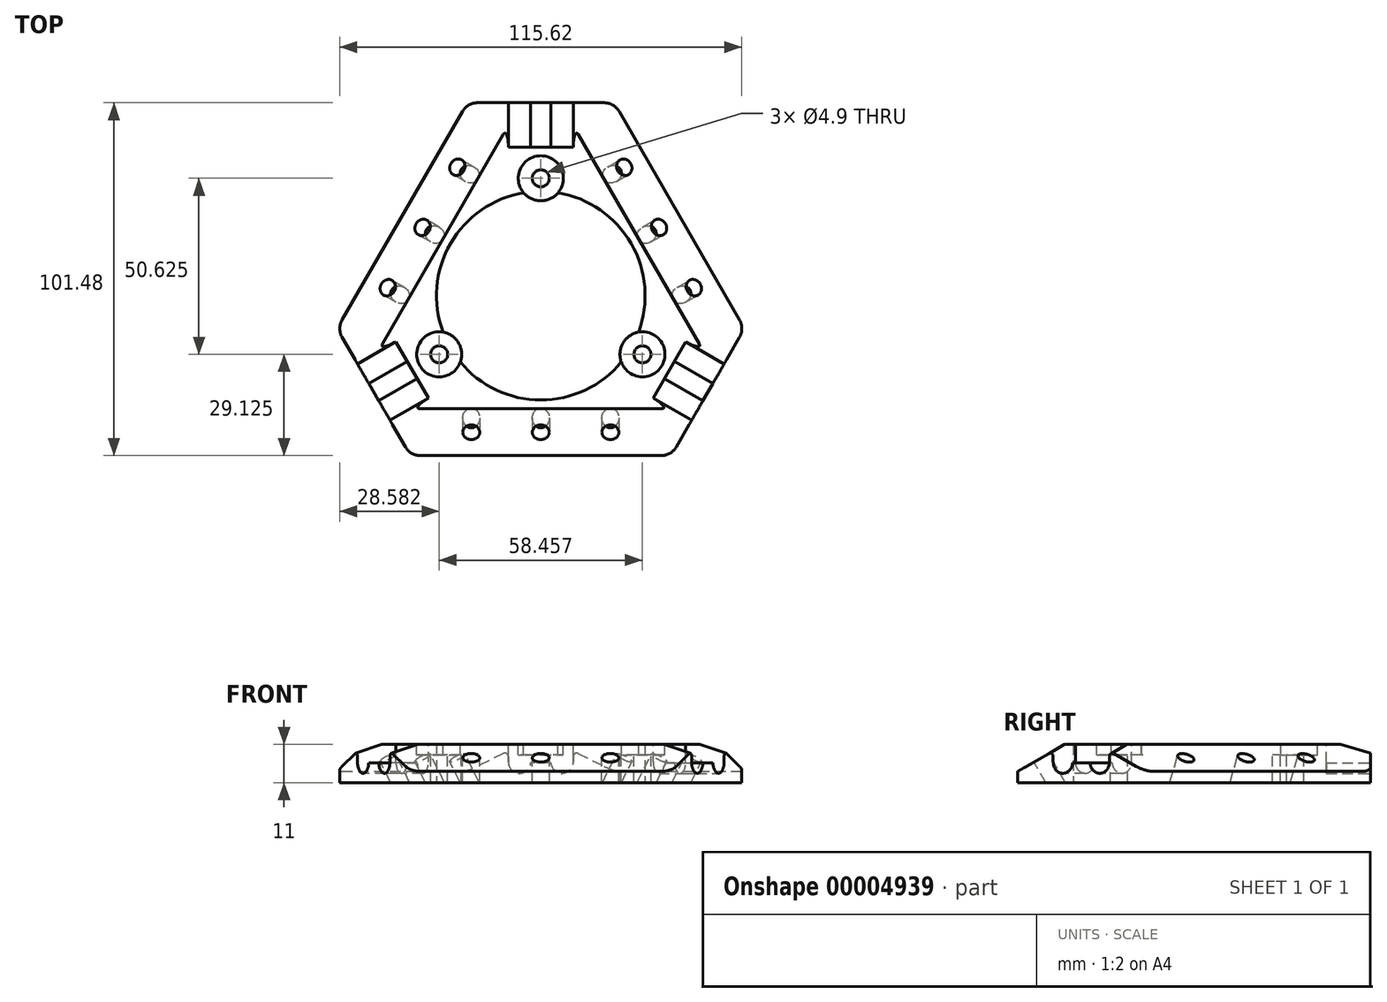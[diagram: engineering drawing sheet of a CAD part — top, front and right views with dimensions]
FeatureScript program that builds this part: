
annotation { "Feature Type Name" : "Feature", "Feature Type Description" : "" }
export const myFeature = defineFeature(function(context is Context, id is Id, definition is map)
    precondition{}
    {
        {
            var Q0;
            Q0=qCreatedBy(makeId("Top.planeOp"),FACE);
            var sketch = newSketch(context, id + "F0", { "sketchPlane" : qUnion([Q0])});
            skArc(sketch, "E0", {"start": v(-25.98, -15) * mm, "mid": v(0, -30) * mm, "end": v(25.98, -15) * mm});
            skLineSegment(sketch, "E1", {"start": v(-37.5, -46) * mm, "end": v(37.5, -46) * mm});
            skLineSegment(sketch, "E2", {"start": v(37.5, -46) * mm, "end": v(48.04, -27.74) * mm});
            skLineSegment(sketch, "E3", {"start": v(48.04, -27.74) * mm, "end": v(25.98, -15) * mm});
            skLineSegment(sketch, "E4", {"start": v(25.98, -15) * mm, "end": v(0, 0) * mm, "construction": true});
            skLineSegment(sketch, "E5", {"start": v(0, 0) * mm, "end": v(0, -46) * mm, "construction": true});
            skLineSegment(sketch, "E6.0.MirrorCS", {"start": v(-37.5, -46) * mm, "end": v(-48.04, -27.74) * mm});
            skLineSegment(sketch, "E6.1.MirrorCS", {"start": v(-48.04, -27.74) * mm, "end": v(-25.98, -15) * mm});
            skPoint(sketch, "E7", {"position": v(0, -30) * mm});
            skSolve(sketch);
        }
        {
            var Q0;
            Q0 = qSketchRegion(id + "F0", true);
            extrude(context, id + "F1", {"entities" : qUnion([Q0]), "depth" : 8 * mm, "symmetric" : true});
        }
        {
            var Q0;
            Q0=qCreatedBy(makeId("Right.planeOp"),FACE);
            var sketch = newSketch(context, id + "F2", { "sketchPlane" : qUnion([Q0])});
            skLineSegment(sketch, "E8", {"start": v(0, 0) * mm, "end": v(-39.45, 0) * mm, "construction": true});
            skLineSegment(sketch, "E9", {"start": v(-46.38, -4) * mm, "end": v(-32.52, 4) * mm});
            skLineSegment(sketch, "E10.0", {"start": v(-46, 4) * mm, "end": v(-32.52, 4) * mm});
            skLineSegment(sketch, "E11", {"start": v(-46, 4) * mm, "end": v(-46.38, 4) * mm});
            skLineSegment(sketch, "E12", {"start": v(-46.38, 4) * mm, "end": v(-46.38, -4) * mm});
            skPoint(sketch, "E13.orphan", {"position": v(-27.74, 4) * mm});
            skSolve(sketch);
        }
        {
            var Q0;
            Q0 = qSketchRegion(id + "F2", true);
            extrude(context, id + "F3", {"entities" : qUnion([Q0]), "operationType" : NewBodyOperationType.REMOVE, "oppositeDirection" : true, "depth" : 100 * mm, "symmetric" : true});
        }
        {
            var Q0;
            Q0=makeQuery(id+"F1.opExtrude","CAP_FACE",FACE,{"disambiguationData":[OSD([sQuery(id+"F0.wireOp",EDGE,"E0"),sQuery(id+"F0.wireOp",EDGE,"E1"),sQuery(id+"F0.wireOp",EDGE,"E2"),sQuery(id+"F0.wireOp",EDGE,"E3"),sQuery(id+"F0.wireOp",EDGE,"E6.0.MirrorCS"),sQuery(id+"F0.wireOp",EDGE,"E6.1.MirrorCS")])],"isStart":true});
            var sketch = newSketch(context, id + "F4", { "sketchPlane" : qUnion([Q0])});
            skLineSegment(sketch, "E14.0", {"start": v(-37.5, 46) * mm, "end": v(-48.04, 27.74) * mm});
            skLineSegment(sketch, "E14.1", {"start": v(-37.5, 46) * mm, "end": v(37.5, 46) * mm});
            skLineSegment(sketch, "E14.2", {"start": v(37.5, 46) * mm, "end": v(48.04, 27.74) * mm});
            skLineSegment(sketch, "E14.3", {"start": v(48.04, 27.74) * mm, "end": v(25.98, 15) * mm});
            skArc(sketch, "E14.4", {"start": v(-25.98, 15) * mm, "mid": v(0, 30) * mm, "end": v(25.98, 15) * mm});
            skLineSegment(sketch, "E14.5", {"start": v(-48.04, 27.74) * mm, "end": v(-25.98, 15) * mm});
            skSolve(sketch);
        }
        {
            var Q0;
            Q0 = qSketchRegion(id + "F4", true);
            extrude(context, id + "F5", {"entities" : qUnion([Q0]), "operationType" : NewBodyOperationType.ADD, "depth" : 3 * mm});
        }
        {
            var Q0;
            Q0=makeQuery(id+"F3.boolean.opBoolean","COPY",FACE,{"derivedFrom":makeQuery(id+"F3.opExtrude","SWEPT_FACE",FACE,{"disambiguationData":[OSD([sQuery(id+"F2.wireOp",EDGE,"E9")])]})});
            var sketch = newSketch(context, id + "F6", { "sketchPlane" : qUnion([Q0])});
            skLineSegment(sketch, "E15", {"start": v(0, -26.16) * mm, "end": v(0, -41.73) * mm, "construction": true});
            skLineSegment(sketch, "E16", {"start": v(0, -33.95) * mm, "end": v(20, -33.95) * mm, "construction": true});
            skCircle(sketch, "E17", {"center": v(20, -33.95) * mm, "radius": 2.45 * mm});
            skCircle(sketch, "E18.0.MirrorC", {"center": v(-20, -33.95) * mm, "radius": 2.45 * mm});
            skCircle(sketch, "E19", {"center": v(0, -33.95) * mm, "radius": 2.45 * mm});
            skSolve(sketch);
        }
        {
            var Q0;
            Q0 = qSketchRegion(id + "F6", true);
            extrude(context, id + "F7", {"entities" : qUnion([Q0]), "operationType" : NewBodyOperationType.REMOVE, "endBound" : BoundingType.THROUGH_ALL, "oppositeDirection" : true, "depth" : 25 * mm});
        }
        {
            var Q0;
            Q0=makeQuery(id+"F5.boolean.opBoolean","MERGE",FACE,{"derivedFrom":[makeQuery(id+"F1.opExtrude","SWEPT_FACE",FACE,{"disambiguationData":[OSD([sQuery(id+"F0.wireOp",EDGE,"E2")])]}),makeQuery(id+"F5.opExtrude","SWEPT_FACE",FACE,{"disambiguationData":[OSD([sQuery(id+"F4.wireOp",EDGE,"E14.2")])]})]});
            var sketch = newSketch(context, id + "F8", { "sketchPlane" : qUnion([Q0])});
            skCircle(sketch, "E20", {"center": v(-6.1, -1.13) * mm, "radius": 3.23 * mm});
            skPoint(sketch, "E21", {"position": v(-6.1, 2.1) * mm});
            skCircle(sketch, "E22", {"center": v(0, 4) * mm, "radius": 4.75 * mm, "construction": true});
            skLineSegment(sketch, "E23", {"start": v(-6.1, -1.13) * mm, "end": v(0, 4) * mm, "construction": true});
            skSolve(sketch);
        }
        {
            var Q0;
            Q0 = qSketchRegion(id + "F8", true);
            extrude(context, id + "F9", {"entities" : qUnion([Q0]), "operationType" : NewBodyOperationType.REMOVE, "oppositeDirection" : true, "depth" : 12.75 * mm});
        }
        {
            var Q0;
            Q0=makeQuery(id+"F5.boolean.opBoolean","MERGE",FACE,{"derivedFrom":[makeQuery(id+"F1.opExtrude","SWEPT_FACE",FACE,{"disambiguationData":[OSD([sQuery(id+"F0.wireOp",EDGE,"E2")])]}),makeQuery(id+"F5.opExtrude","SWEPT_FACE",FACE,{"disambiguationData":[OSD([sQuery(id+"F4.wireOp",EDGE,"E14.2")])]})]});
            var sketch = newSketch(context, id + "F10", { "sketchPlane" : qUnion([Q0])});
            skPoint(sketch, "E24", {"position": v(-6.1, -4.35) * mm});
            skPoint(sketch, "E25", {"position": v(-6.1, -1.13) * mm});
            skArc(sketch, "E26.0", {"start": v(-2.9, -1.35) * mm, "mid": v(-6, 2.1) * mm, "end": v(-9.33, -1.13) * mm});
            skLineSegment(sketch, "E27", {"start": v(-2.9, -1.35) * mm, "end": v(0, -1.35) * mm});
            skLineSegment(sketch, "E28", {"start": v(0, -1.35) * mm, "end": v(0, 4) * mm});
            skLineSegment(sketch, "E29", {"start": v(0, 4) * mm, "end": v(-5.52, 4) * mm});
            skLineSegment(sketch, "E30", {"start": v(-5.52, 4) * mm, "end": v(-9.33, 2.1) * mm, "construction": true});
            skLineSegment(sketch, "E31", {"start": v(-9.33, 2.1) * mm, "end": v(-9.33, -1.13) * mm});
            skLineSegment(sketch, "E32", {"start": v(-5.52, 4) * mm, "end": v(-9.33, 4) * mm});
            skLineSegment(sketch, "E33", {"start": v(-9.33, 4) * mm, "end": v(-9.33, 2.1) * mm});
            skSolve(sketch);
        }
        {
            var Q0;
            Q0 = qSketchRegion(id + "F10", true);
            var Q1;
            Q1=makeQuery(id+"F9.boolean.opBoolean","COPY",FACE,{"derivedFrom":makeQuery(id+"F9.opExtrude","CAP_FACE",FACE,{"disambiguationData":[OSD([sQuery(id+"F8.wireOp",EDGE,"E20")])],"isStart":false})});
            extrude(context, id + "F11", {"entities" : qUnion([Q0]), "operationType" : NewBodyOperationType.REMOVE, "endBound" : BoundingType.UP_TO_SURFACE, "oppositeDirection" : true, "endBoundEntityFace" : qUnion([Q1]), "depth" : 25 * mm});
        }
        {
            var Q0;
            Q0=makeQuery(id+"F5.boolean.opBoolean","MERGE",FACE,{"derivedFrom":[makeQuery(id+"F1.opExtrude","SWEPT_FACE",FACE,{"disambiguationData":[OSD([sQuery(id+"F0.wireOp",EDGE,"E6.0.MirrorCS")])]}),makeQuery(id+"F5.opExtrude","SWEPT_FACE",FACE,{"disambiguationData":[OSD([sQuery(id+"F4.wireOp",EDGE,"E14.0")])]})]});
            var sketch = newSketch(context, id + "F12", { "sketchPlane" : qUnion([Q0])});
            skCircle(sketch, "E34", {"center": v(0, 4) * mm, "radius": 4.75 * mm, "construction": true});
            skCircle(sketch, "E35", {"center": v(6.1, -1.13) * mm, "radius": 3.23 * mm});
            skLineSegment(sketch, "E36", {"start": v(0, 4) * mm, "end": v(6.1, -1.13) * mm, "construction": true});
            skSolve(sketch);
        }
        {
            var Q0;
            Q0 = qSketchRegion(id + "F12", true);
            extrude(context, id + "F13", {"entities" : qUnion([Q0]), "operationType" : NewBodyOperationType.REMOVE, "oppositeDirection" : true, "depth" : 12.75 * mm});
        }
        {
            var Q0;
            Q0=makeQuery(id+"F5.boolean.opBoolean","MERGE",FACE,{"derivedFrom":[makeQuery(id+"F1.opExtrude","SWEPT_FACE",FACE,{"disambiguationData":[OSD([sQuery(id+"F0.wireOp",EDGE,"E6.0.MirrorCS")])]}),makeQuery(id+"F5.opExtrude","SWEPT_FACE",FACE,{"disambiguationData":[OSD([sQuery(id+"F4.wireOp",EDGE,"E14.0")])]})]});
            var sketch = newSketch(context, id + "F14", { "sketchPlane" : qUnion([Q0])});
            skArc(sketch, "E37.0", {"start": v(9.33, -1.13) * mm, "mid": v(6, 2.1) * mm, "end": v(2.9, -1.35) * mm});
            skPoint(sketch, "E38", {"position": v(6.1, -4.35) * mm});
            skLineSegment(sketch, "E39", {"start": v(2.9, -1.35) * mm, "end": v(0, -1.35) * mm});
            skLineSegment(sketch, "E40", {"start": v(0, -1.35) * mm, "end": v(0, 4) * mm});
            skLineSegment(sketch, "E41", {"start": v(0, 4) * mm, "end": v(9.33, 4) * mm});
            skLineSegment(sketch, "E42", {"start": v(9.33, 4) * mm, "end": v(9.33, -1.13) * mm});
            skSolve(sketch);
        }
        {
            var Q0;
            Q0 = qSketchRegion(id + "F14", true);
            var Q1;
            Q1=makeQuery(id+"F13.boolean.opBoolean","COPY",FACE,{"derivedFrom":makeQuery(id+"F13.opExtrude","CAP_FACE",FACE,{"disambiguationData":[OSD([sQuery(id+"F12.wireOp",EDGE,"E35")])],"isStart":false})});
            extrude(context, id + "F15", {"entities" : qUnion([Q0]), "operationType" : NewBodyOperationType.REMOVE, "endBound" : BoundingType.UP_TO_SURFACE, "oppositeDirection" : true, "endBoundEntityFace" : qUnion([Q1]), "depth" : 25 * mm});
        }
        {
            var Q0;
            Q0=makeQuery(id+"F1.opExtrude","SWEPT_BODY",BODY,{"disambiguationData":[OSD([sQuery(id+"F0.wireOp",EDGE,"E0"),sQuery(id+"F0.wireOp",EDGE,"E1"),sQuery(id+"F0.wireOp",EDGE,"E2"),sQuery(id+"F0.wireOp",EDGE,"E3"),sQuery(id+"F0.wireOp",EDGE,"E6.0.MirrorCS"),sQuery(id+"F0.wireOp",EDGE,"E6.1.MirrorCS")])]});
            var Q1;
            Q1=makeQuery(id+"F1.opExtrude","CAP_EDGE",EDGE,{"disambiguationData":[OSD([sQuery(id+"F0.wireOp",EDGE,"E0")])],"isStart":false});
            circularPattern(context, id + "F16", {"entities" : qUnion([Q0]), "axis" : qUnion([Q1]), "angle" : 360 * degree, "instanceCount" : 3, "equalSpace" : true});
        }
        {
            var Q0;
            Q0=makeQuery(id+"F1.opExtrude","SWEPT_BODY",BODY,{"disambiguationData":[OSD([sQuery(id+"F0.wireOp",EDGE,"E0"),sQuery(id+"F0.wireOp",EDGE,"E1"),sQuery(id+"F0.wireOp",EDGE,"E2"),sQuery(id+"F0.wireOp",EDGE,"E3"),sQuery(id+"F0.wireOp",EDGE,"E6.0.MirrorCS"),sQuery(id+"F0.wireOp",EDGE,"E6.1.MirrorCS")])]});
            var Q1;
            Q1=makeQuery(id+"F16.opPattern","COPY",BODY,{"derivedFrom":makeQuery(id+"F1.opExtrude","SWEPT_BODY",BODY,{"disambiguationData":[OSD([sQuery(id+"F0.wireOp",EDGE,"E0"),sQuery(id+"F0.wireOp",EDGE,"E1"),sQuery(id+"F0.wireOp",EDGE,"E2"),sQuery(id+"F0.wireOp",EDGE,"E3"),sQuery(id+"F0.wireOp",EDGE,"E6.0.MirrorCS"),sQuery(id+"F0.wireOp",EDGE,"E6.1.MirrorCS")])]}),"instanceName":"1"});
            var Q2;
            Q2=makeQuery(id+"F16.opPattern","COPY",BODY,{"derivedFrom":makeQuery(id+"F1.opExtrude","SWEPT_BODY",BODY,{"disambiguationData":[OSD([sQuery(id+"F0.wireOp",EDGE,"E0"),sQuery(id+"F0.wireOp",EDGE,"E1"),sQuery(id+"F0.wireOp",EDGE,"E2"),sQuery(id+"F0.wireOp",EDGE,"E3"),sQuery(id+"F0.wireOp",EDGE,"E6.0.MirrorCS"),sQuery(id+"F0.wireOp",EDGE,"E6.1.MirrorCS")])]}),"instanceName":"2"});
            booleanBodies(context, id + "F17", {"operationType" : BooleanOperationType.UNION, "tools" : qUnion([Q0, Q1, Q2])});
        }
        {
            var Q0;
            {var subQ0=makeQuery(id+"F1.opExtrude","CAP_FACE",FACE,{"disambiguationData":[OSD([sQuery(id+"F0.wireOp",EDGE,"E0"),sQuery(id+"F0.wireOp",EDGE,"E1"),sQuery(id+"F0.wireOp",EDGE,"E2"),sQuery(id+"F0.wireOp",EDGE,"E3"),sQuery(id+"F0.wireOp",EDGE,"E6.0.MirrorCS"),sQuery(id+"F0.wireOp",EDGE,"E6.1.MirrorCS")])],"isStart":false});Q0=makeQuery(id+"F17.opBoolean","MERGE",FACE,{"derivedFrom":[subQ0,makeQuery(id+"F16.opPattern","COPY",FACE,{"derivedFrom":subQ0,"instanceName":"1"}),makeQuery(id+"F16.opPattern","COPY",FACE,{"derivedFrom":subQ0,"instanceName":"2"})]});}
            var sketch = newSketch(context, id + "F18", { "sketchPlane" : qUnion([Q0])});
            skLineSegment(sketch, "E43", {"start": v(0, 0) * mm, "end": v(37, -21.36) * mm, "construction": true});
            skCircle(sketch, "E44", {"center": v(29.23, -16.87) * mm, "radius": 6.47 * mm});
            skPoint(sketch, "E45", {"position": v(34.84, -20.11) * mm});
            skCircle(sketch, "E46.1.0", {"center": v(0, 33.75) * mm, "radius": 6.47 * mm});
            skCircle(sketch, "E46.2.0", {"center": v(-29.23, -16.88) * mm, "radius": 6.47 * mm});
            skPoint(sketch, "E46.center", {"position": v(0, 0) * mm});
            skSolve(sketch);
        }
        {
            var Q0;
            Q0 = qSketchRegion(id + "F18", true);
            var Q1;
            {var subQ0=makeQuery(id+"F5.opExtrude","CAP_FACE",FACE,{"disambiguationData":[OSD([sQuery(id+"F4.wireOp",EDGE,"E14.0"),sQuery(id+"F4.wireOp",EDGE,"E14.1"),sQuery(id+"F4.wireOp",EDGE,"E14.2"),sQuery(id+"F4.wireOp",EDGE,"E14.3"),sQuery(id+"F4.wireOp",EDGE,"E14.4"),sQuery(id+"F4.wireOp",EDGE,"E14.5")])],"isStart":false});Q1=makeQuery(id+"F17.opBoolean","MERGE",FACE,{"derivedFrom":[subQ0,makeQuery(id+"F16.opPattern","COPY",FACE,{"derivedFrom":subQ0,"instanceName":"1"}),makeQuery(id+"F16.opPattern","COPY",FACE,{"derivedFrom":subQ0,"instanceName":"2"})]});}
            extrude(context, id + "F19", {"entities" : qUnion([Q0]), "operationType" : NewBodyOperationType.ADD, "endBound" : BoundingType.UP_TO_SURFACE, "oppositeDirection" : true, "endBoundEntityFace" : qUnion([Q1]), "depth" : 25 * mm});
        }
        {
            var Q0;
            {var subQ0=makeQuery(id+"F1.opExtrude","CAP_FACE",FACE,{"disambiguationData":[OSD([sQuery(id+"F0.wireOp",EDGE,"E0"),sQuery(id+"F0.wireOp",EDGE,"E1"),sQuery(id+"F0.wireOp",EDGE,"E2"),sQuery(id+"F0.wireOp",EDGE,"E3"),sQuery(id+"F0.wireOp",EDGE,"E6.0.MirrorCS"),sQuery(id+"F0.wireOp",EDGE,"E6.1.MirrorCS")])],"isStart":false});Q0=makeQuery(id+"F19.boolean.opBoolean","MERGE",FACE,{"derivedFrom":[makeQuery(id+"F17.opBoolean","MERGE",FACE,{"derivedFrom":[subQ0,makeQuery(id+"F16.opPattern","COPY",FACE,{"derivedFrom":subQ0,"instanceName":"1"}),makeQuery(id+"F16.opPattern","COPY",FACE,{"derivedFrom":subQ0,"instanceName":"2"})]}),makeQuery(id+"F19.opExtrude","CAP_FACE",FACE,{"disambiguationData":[OSD([sQuery(id+"F18.wireOp",EDGE,"E44")])],"isStart":true}),makeQuery(id+"F19.opExtrude","CAP_FACE",FACE,{"disambiguationData":[OSD([sQuery(id+"F18.wireOp",EDGE,"E46.1.0")])],"isStart":true}),makeQuery(id+"F19.opExtrude","CAP_FACE",FACE,{"disambiguationData":[OSD([sQuery(id+"F18.wireOp",EDGE,"E46.2.0")])],"isStart":true})]});}
            var sketch = newSketch(context, id + "F20", { "sketchPlane" : qUnion([Q0])});
            skCircle(sketch, "E47", {"center": v(29.23, -16.87) * mm, "radius": 6.48 * mm});
            skCircle(sketch, "E48.1.0", {"center": v(0, 33.75) * mm, "radius": 6.48 * mm});
            skCircle(sketch, "E48.2.0", {"center": v(-29.23, -16.88) * mm, "radius": 6.48 * mm});
            skPoint(sketch, "E48.center", {"position": v(0, 0) * mm});
            skSolve(sketch);
        }
        {
            var Q0;
            Q0 = qSketchRegion(id + "F20", true);
            extrude(context, id + "F21", {"entities" : qUnion([Q0]), "operationType" : NewBodyOperationType.REMOVE, "oppositeDirection" : true, "depth" : 3 * mm});
        }
        {
            var Q0;
            Q0=makeQuery(id+"F16.opPattern","COPY",EDGE,{"derivedFrom":makeQuery(id+"F11.boolean.opBoolean","COPY",EDGE,{"derivedFrom":makeQuery(id+"F11.opExtrude","SWEPT_EDGE",EDGE,{"disambiguationData":[OSD([sQuery(id+"F8.wireOp",EDGE,"E20"),sQuery(id+"F10.wireOp",EDGE,"E26.0"),sQuery(id+"F10.wireOp",EDGE,"E27")])]})}),"instanceName":"2"});
            var Q1;
            Q1=makeQuery(id+"F15.boolean.opBoolean","COPY",EDGE,{"derivedFrom":makeQuery(id+"F15.opExtrude","SWEPT_EDGE",EDGE,{"disambiguationData":[OSD([sQuery(id+"F12.wireOp",EDGE,"E35"),sQuery(id+"F14.wireOp",EDGE,"E37.0"),sQuery(id+"F14.wireOp",EDGE,"E39")])]})});
            var Q2;
            {var subQ0=sQuery(id+"F0.wireOp",EDGE,"E0");var subQ1=makeQuery(id+"F1.opExtrude","SWEPT_FACE",FACE,{"disambiguationData":[OSD([subQ0])]});var subQ2=makeQuery(id+"F5.opExtrude","SWEPT_FACE",FACE,{"disambiguationData":[OSD([sQuery(id+"F4.wireOp",EDGE,"E14.4")])]});var subQ3=makeQuery(id+"F5.boolean.opBoolean","MERGE",FACE,{"derivedFrom":[subQ1,subQ2]});var subQ4=makeQuery(id+"F16.opPattern","COPY",FACE,{"derivedFrom":subQ3,"instanceName":"1"});var subQ5=makeQuery(id+"F16.opPattern","COPY",FACE,{"derivedFrom":subQ3,"instanceName":"2"});var subQ6=sQuery(id+"F18.wireOp",EDGE,"E46.2.0");var subQ7=makeQuery(id+"F19.opExtrude","SWEPT_FACE",FACE,{"disambiguationData":[OSD([subQ6])]});Q2=makeQuery(id+"F21.boolean.opBoolean","SPLIT",EDGE,{"disambiguationData":[TD([makeQuery(id+"F19.opExtrude","CAP_FACE",FACE,{"disambiguationData":[OSD([sQuery(id+"F18.wireOp",EDGE,"E44")])],"isStart":true})])],"derivedFrom":makeQuery(id+"F19.boolean.opBoolean","INTERSECT",EDGE,{"disambiguationData":[OD(0.0)],"derivedFrom":[makeQuery(id+"F17.opBoolean","MERGE",FACE,{"derivedFrom":[subQ3,subQ4,subQ5]}),subQ7]})});}
            var Q3;
            {var subQ0=sQuery(id+"F0.wireOp",EDGE,"E0");var subQ1=makeQuery(id+"F1.opExtrude","SWEPT_FACE",FACE,{"disambiguationData":[OSD([subQ0])]});var subQ2=makeQuery(id+"F5.opExtrude","SWEPT_FACE",FACE,{"disambiguationData":[OSD([sQuery(id+"F4.wireOp",EDGE,"E14.4")])]});var subQ3=makeQuery(id+"F5.boolean.opBoolean","MERGE",FACE,{"derivedFrom":[subQ1,subQ2]});var subQ4=makeQuery(id+"F16.opPattern","COPY",FACE,{"derivedFrom":subQ3,"instanceName":"1"});var subQ5=makeQuery(id+"F16.opPattern","COPY",FACE,{"derivedFrom":subQ3,"instanceName":"2"});var subQ6=sQuery(id+"F18.wireOp",EDGE,"E46.2.0");var subQ7=makeQuery(id+"F19.opExtrude","SWEPT_FACE",FACE,{"disambiguationData":[OSD([subQ6])]});Q3=makeQuery(id+"F21.boolean.opBoolean","SPLIT",EDGE,{"disambiguationData":[TD([makeQuery(id+"F19.opExtrude","CAP_FACE",FACE,{"disambiguationData":[OSD([sQuery(id+"F18.wireOp",EDGE,"E44")])],"isStart":true})])],"derivedFrom":makeQuery(id+"F19.boolean.opBoolean","INTERSECT",EDGE,{"disambiguationData":[OD(1.0)],"derivedFrom":[makeQuery(id+"F17.opBoolean","MERGE",FACE,{"derivedFrom":[subQ3,subQ4,subQ5]}),subQ7]})});}
            var Q4;
            {var subQ0=sQuery(id+"F0.wireOp",EDGE,"E0");var subQ1=makeQuery(id+"F1.opExtrude","SWEPT_FACE",FACE,{"disambiguationData":[OSD([subQ0])]});var subQ2=makeQuery(id+"F5.opExtrude","SWEPT_FACE",FACE,{"disambiguationData":[OSD([sQuery(id+"F4.wireOp",EDGE,"E14.4")])]});var subQ3=makeQuery(id+"F5.boolean.opBoolean","MERGE",FACE,{"derivedFrom":[subQ1,subQ2]});var subQ4=makeQuery(id+"F16.opPattern","COPY",FACE,{"derivedFrom":subQ3,"instanceName":"1"});var subQ5=makeQuery(id+"F16.opPattern","COPY",FACE,{"derivedFrom":subQ3,"instanceName":"2"});var subQ6=sQuery(id+"F18.wireOp",EDGE,"E46.1.0");var subQ7=makeQuery(id+"F19.opExtrude","SWEPT_FACE",FACE,{"disambiguationData":[OSD([subQ6])]});Q4=makeQuery(id+"F21.boolean.opBoolean","SPLIT",EDGE,{"disambiguationData":[TD([makeQuery(id+"F19.opExtrude","CAP_FACE",FACE,{"disambiguationData":[OSD([sQuery(id+"F18.wireOp",EDGE,"E44")])],"isStart":true})])],"derivedFrom":makeQuery(id+"F19.boolean.opBoolean","INTERSECT",EDGE,{"disambiguationData":[OD(1.0)],"derivedFrom":[makeQuery(id+"F17.opBoolean","MERGE",FACE,{"derivedFrom":[subQ3,subQ4,subQ5]}),subQ7]})});}
            var Q5;
            {var subQ0=sQuery(id+"F0.wireOp",EDGE,"E0");var subQ1=makeQuery(id+"F1.opExtrude","SWEPT_FACE",FACE,{"disambiguationData":[OSD([subQ0])]});var subQ2=makeQuery(id+"F5.opExtrude","SWEPT_FACE",FACE,{"disambiguationData":[OSD([sQuery(id+"F4.wireOp",EDGE,"E14.4")])]});var subQ3=makeQuery(id+"F5.boolean.opBoolean","MERGE",FACE,{"derivedFrom":[subQ1,subQ2]});var subQ4=makeQuery(id+"F16.opPattern","COPY",FACE,{"derivedFrom":subQ3,"instanceName":"1"});var subQ5=makeQuery(id+"F16.opPattern","COPY",FACE,{"derivedFrom":subQ3,"instanceName":"2"});var subQ6=sQuery(id+"F18.wireOp",EDGE,"E46.1.0");var subQ7=makeQuery(id+"F19.opExtrude","SWEPT_FACE",FACE,{"disambiguationData":[OSD([subQ6])]});Q5=makeQuery(id+"F21.boolean.opBoolean","SPLIT",EDGE,{"disambiguationData":[TD([makeQuery(id+"F19.opExtrude","CAP_FACE",FACE,{"disambiguationData":[OSD([sQuery(id+"F18.wireOp",EDGE,"E44")])],"isStart":true})])],"derivedFrom":makeQuery(id+"F19.boolean.opBoolean","INTERSECT",EDGE,{"disambiguationData":[OD(0.0)],"derivedFrom":[makeQuery(id+"F17.opBoolean","MERGE",FACE,{"derivedFrom":[subQ3,subQ4,subQ5]}),subQ7]})});}
            var Q6;
            {var subQ0=sQuery(id+"F0.wireOp",EDGE,"E0");var subQ1=makeQuery(id+"F1.opExtrude","SWEPT_FACE",FACE,{"disambiguationData":[OSD([subQ0])]});var subQ2=makeQuery(id+"F5.opExtrude","SWEPT_FACE",FACE,{"disambiguationData":[OSD([sQuery(id+"F4.wireOp",EDGE,"E14.4")])]});var subQ3=makeQuery(id+"F5.boolean.opBoolean","MERGE",FACE,{"derivedFrom":[subQ1,subQ2]});var subQ4=makeQuery(id+"F16.opPattern","COPY",FACE,{"derivedFrom":subQ3,"instanceName":"1"});var subQ5=makeQuery(id+"F16.opPattern","COPY",FACE,{"derivedFrom":subQ3,"instanceName":"2"});var subQ6=sQuery(id+"F18.wireOp",EDGE,"E44");var subQ7=makeQuery(id+"F19.opExtrude","SWEPT_FACE",FACE,{"disambiguationData":[OSD([subQ6])]});Q6=makeQuery(id+"F21.boolean.opBoolean","SPLIT",EDGE,{"disambiguationData":[TD([makeQuery(id+"F19.opExtrude","CAP_FACE",FACE,{"disambiguationData":[OSD([subQ6])],"isStart":true})])],"derivedFrom":makeQuery(id+"F19.boolean.opBoolean","INTERSECT",EDGE,{"disambiguationData":[OD(0.0)],"derivedFrom":[makeQuery(id+"F17.opBoolean","MERGE",FACE,{"derivedFrom":[subQ3,subQ4,subQ5]}),subQ7]})});}
            var Q7;
            {var subQ0=sQuery(id+"F0.wireOp",EDGE,"E0");var subQ1=makeQuery(id+"F1.opExtrude","SWEPT_FACE",FACE,{"disambiguationData":[OSD([subQ0])]});var subQ2=makeQuery(id+"F5.opExtrude","SWEPT_FACE",FACE,{"disambiguationData":[OSD([sQuery(id+"F4.wireOp",EDGE,"E14.4")])]});var subQ3=makeQuery(id+"F5.boolean.opBoolean","MERGE",FACE,{"derivedFrom":[subQ1,subQ2]});var subQ4=makeQuery(id+"F16.opPattern","COPY",FACE,{"derivedFrom":subQ3,"instanceName":"1"});var subQ5=makeQuery(id+"F16.opPattern","COPY",FACE,{"derivedFrom":subQ3,"instanceName":"2"});var subQ6=sQuery(id+"F18.wireOp",EDGE,"E44");var subQ7=makeQuery(id+"F19.opExtrude","SWEPT_FACE",FACE,{"disambiguationData":[OSD([subQ6])]});Q7=makeQuery(id+"F21.boolean.opBoolean","SPLIT",EDGE,{"disambiguationData":[TD([makeQuery(id+"F19.opExtrude","CAP_FACE",FACE,{"disambiguationData":[OSD([subQ6])],"isStart":true})])],"derivedFrom":makeQuery(id+"F19.boolean.opBoolean","INTERSECT",EDGE,{"disambiguationData":[OD(1.0)],"derivedFrom":[makeQuery(id+"F17.opBoolean","MERGE",FACE,{"derivedFrom":[subQ3,subQ4,subQ5]}),subQ7]})});}
            var Q8;
            Q8=makeQuery(id+"F11.boolean.opBoolean","COPY",EDGE,{"derivedFrom":makeQuery(id+"F11.opExtrude","SWEPT_EDGE",EDGE,{"disambiguationData":[OSD([sQuery(id+"F8.wireOp",EDGE,"E20"),sQuery(id+"F10.wireOp",EDGE,"E26.0"),sQuery(id+"F10.wireOp",EDGE,"E27")])]})});
            var Q9;
            Q9=makeQuery(id+"F16.opPattern","COPY",EDGE,{"derivedFrom":makeQuery(id+"F15.boolean.opBoolean","COPY",EDGE,{"derivedFrom":makeQuery(id+"F15.opExtrude","SWEPT_EDGE",EDGE,{"disambiguationData":[OSD([sQuery(id+"F12.wireOp",EDGE,"E35"),sQuery(id+"F14.wireOp",EDGE,"E37.0"),sQuery(id+"F14.wireOp",EDGE,"E39")])]})}),"instanceName":"1"});
            var Q10;
            Q10=makeQuery(id+"F16.opPattern","COPY",EDGE,{"derivedFrom":makeQuery(id+"F15.boolean.opBoolean","COPY",EDGE,{"derivedFrom":makeQuery(id+"F15.opExtrude","SWEPT_EDGE",EDGE,{"disambiguationData":[OSD([sQuery(id+"F12.wireOp",EDGE,"E35"),sQuery(id+"F14.wireOp",EDGE,"E37.0"),sQuery(id+"F14.wireOp",EDGE,"E39")])]})}),"instanceName":"2"});
            var Q11;
            Q11=makeQuery(id+"F16.opPattern","COPY",EDGE,{"derivedFrom":makeQuery(id+"F11.boolean.opBoolean","COPY",EDGE,{"derivedFrom":makeQuery(id+"F11.opExtrude","SWEPT_EDGE",EDGE,{"disambiguationData":[OSD([sQuery(id+"F8.wireOp",EDGE,"E20"),sQuery(id+"F10.wireOp",EDGE,"E26.0"),sQuery(id+"F10.wireOp",EDGE,"E27")])]})}),"instanceName":"1"});
            var Q12;
            Q12=makeQuery(id+"F16.opPattern","COPY",EDGE,{"derivedFrom":makeQuery(id+"F11.boolean.opBoolean","INTERSECT",EDGE,{"derivedFrom":[makeQuery(id+"F3.boolean.opBoolean","COPY",FACE,{"derivedFrom":makeQuery(id+"F3.opExtrude","SWEPT_FACE",FACE,{"disambiguationData":[OSD([sQuery(id+"F2.wireOp",EDGE,"E9")])]})}),makeQuery(id+"F11.opExtrude","SWEPT_FACE",FACE,{"disambiguationData":[OSD([sQuery(id+"F10.wireOp",EDGE,"E31"),sQuery(id+"F10.wireOp",EDGE,"E33")])]})]}),"instanceName":"2"});
            var Q13;
            Q13=makeQuery(id+"F16.opPattern","COPY",EDGE,{"derivedFrom":makeQuery(id+"F11.boolean.opBoolean","COPY",EDGE,{"derivedFrom":makeQuery(id+"F11.opExtrude","SWEPT_EDGE",EDGE,{"disambiguationData":[OSD([sQuery(id+"F10.wireOp",EDGE,"E32"),sQuery(id+"F10.wireOp",EDGE,"E33")])]})}),"instanceName":"2"});
            var Q14;
            Q14=makeQuery(id+"F15.boolean.opBoolean","COPY",EDGE,{"derivedFrom":makeQuery(id+"F15.opExtrude","SWEPT_EDGE",EDGE,{"disambiguationData":[OSD([sQuery(id+"F14.wireOp",EDGE,"E41"),sQuery(id+"F14.wireOp",EDGE,"E42")])]})});
            var Q15;
            Q15=makeQuery(id+"F15.boolean.opBoolean","INTERSECT",EDGE,{"derivedFrom":[makeQuery(id+"F3.boolean.opBoolean","COPY",FACE,{"derivedFrom":makeQuery(id+"F3.opExtrude","SWEPT_FACE",FACE,{"disambiguationData":[OSD([sQuery(id+"F2.wireOp",EDGE,"E9")])]})}),makeQuery(id+"F15.opExtrude","SWEPT_FACE",FACE,{"disambiguationData":[OSD([sQuery(id+"F14.wireOp",EDGE,"E42")])]})]});
            var Q16;
            Q16=makeQuery(id+"F16.opPattern","COPY",EDGE,{"derivedFrom":makeQuery(id+"F11.boolean.opBoolean","INTERSECT",EDGE,{"derivedFrom":[makeQuery(id+"F3.boolean.opBoolean","COPY",FACE,{"derivedFrom":makeQuery(id+"F3.opExtrude","SWEPT_FACE",FACE,{"disambiguationData":[OSD([sQuery(id+"F2.wireOp",EDGE,"E9")])]})}),makeQuery(id+"F11.opExtrude","SWEPT_FACE",FACE,{"disambiguationData":[OSD([sQuery(id+"F10.wireOp",EDGE,"E31"),sQuery(id+"F10.wireOp",EDGE,"E33")])]})]}),"instanceName":"1"});
            var Q17;
            Q17=makeQuery(id+"F16.opPattern","COPY",EDGE,{"derivedFrom":makeQuery(id+"F11.boolean.opBoolean","COPY",EDGE,{"derivedFrom":makeQuery(id+"F11.opExtrude","SWEPT_EDGE",EDGE,{"disambiguationData":[OSD([sQuery(id+"F10.wireOp",EDGE,"E32"),sQuery(id+"F10.wireOp",EDGE,"E33")])]})}),"instanceName":"1"});
            var Q18;
            Q18=makeQuery(id+"F16.opPattern","COPY",EDGE,{"derivedFrom":makeQuery(id+"F15.boolean.opBoolean","COPY",EDGE,{"derivedFrom":makeQuery(id+"F15.opExtrude","SWEPT_EDGE",EDGE,{"disambiguationData":[OSD([sQuery(id+"F14.wireOp",EDGE,"E41"),sQuery(id+"F14.wireOp",EDGE,"E42")])]})}),"instanceName":"2"});
            var Q19;
            Q19=makeQuery(id+"F16.opPattern","COPY",EDGE,{"derivedFrom":makeQuery(id+"F15.boolean.opBoolean","INTERSECT",EDGE,{"derivedFrom":[makeQuery(id+"F3.boolean.opBoolean","COPY",FACE,{"derivedFrom":makeQuery(id+"F3.opExtrude","SWEPT_FACE",FACE,{"disambiguationData":[OSD([sQuery(id+"F2.wireOp",EDGE,"E9")])]})}),makeQuery(id+"F15.opExtrude","SWEPT_FACE",FACE,{"disambiguationData":[OSD([sQuery(id+"F14.wireOp",EDGE,"E42")])]})]}),"instanceName":"2"});
            var Q20;
            Q20=makeQuery(id+"F11.boolean.opBoolean","INTERSECT",EDGE,{"derivedFrom":[makeQuery(id+"F3.boolean.opBoolean","COPY",FACE,{"derivedFrom":makeQuery(id+"F3.opExtrude","SWEPT_FACE",FACE,{"disambiguationData":[OSD([sQuery(id+"F2.wireOp",EDGE,"E9")])]})}),makeQuery(id+"F11.opExtrude","SWEPT_FACE",FACE,{"disambiguationData":[OSD([sQuery(id+"F10.wireOp",EDGE,"E31"),sQuery(id+"F10.wireOp",EDGE,"E33")])]})]});
            var Q21;
            Q21=makeQuery(id+"F11.boolean.opBoolean","COPY",EDGE,{"derivedFrom":makeQuery(id+"F11.opExtrude","SWEPT_EDGE",EDGE,{"disambiguationData":[OSD([sQuery(id+"F10.wireOp",EDGE,"E32"),sQuery(id+"F10.wireOp",EDGE,"E33")])]})});
            var Q22;
            Q22=makeQuery(id+"F16.opPattern","COPY",EDGE,{"derivedFrom":makeQuery(id+"F15.boolean.opBoolean","COPY",EDGE,{"derivedFrom":makeQuery(id+"F15.opExtrude","SWEPT_EDGE",EDGE,{"disambiguationData":[OSD([sQuery(id+"F14.wireOp",EDGE,"E41"),sQuery(id+"F14.wireOp",EDGE,"E42")])]})}),"instanceName":"1"});
            var Q23;
            Q23=makeQuery(id+"F16.opPattern","COPY",EDGE,{"derivedFrom":makeQuery(id+"F15.boolean.opBoolean","INTERSECT",EDGE,{"derivedFrom":[makeQuery(id+"F3.boolean.opBoolean","COPY",FACE,{"derivedFrom":makeQuery(id+"F3.opExtrude","SWEPT_FACE",FACE,{"disambiguationData":[OSD([sQuery(id+"F2.wireOp",EDGE,"E9")])]})}),makeQuery(id+"F15.opExtrude","SWEPT_FACE",FACE,{"disambiguationData":[OSD([sQuery(id+"F14.wireOp",EDGE,"E42")])]})]}),"instanceName":"1"});
            fillet(context, id + "F22", {"entities" : qUnion([Q0, Q1, Q2, Q3, Q4, Q5, Q6, Q7, Q8, Q9, Q10, Q11, Q12, Q13, Q14, Q15, Q16, Q17, Q18, Q19, Q20, Q21, Q22, Q23]), "radius" : 1 * mm, "tangentPropagation" : true, "allowEdgeOverflow" : false});
        }
        {
            var Q0;
            Q0=makeQuery(id+"F5.boolean.opBoolean","MERGE",EDGE,{"derivedFrom":[makeQuery(id+"F1.opExtrude","SWEPT_EDGE",EDGE,{"disambiguationData":[OSD([sQuery(id+"F0.wireOp",EDGE,"E1"),sQuery(id+"F0.wireOp",EDGE,"E2")])]}),makeQuery(id+"F5.opExtrude","SWEPT_EDGE",EDGE,{"disambiguationData":[OSD([sQuery(id+"F4.wireOp",EDGE,"E14.1"),sQuery(id+"F4.wireOp",EDGE,"E14.2")])]})]});
            var Q1;
            Q1=makeQuery(id+"F16.opPattern","COPY",EDGE,{"derivedFrom":makeQuery(id+"F5.boolean.opBoolean","MERGE",EDGE,{"derivedFrom":[makeQuery(id+"F1.opExtrude","SWEPT_EDGE",EDGE,{"disambiguationData":[OSD([sQuery(id+"F0.wireOp",EDGE,"E1"),sQuery(id+"F0.wireOp",EDGE,"E6.0.MirrorCS")])]}),makeQuery(id+"F5.opExtrude","SWEPT_EDGE",EDGE,{"disambiguationData":[OSD([sQuery(id+"F4.wireOp",EDGE,"E14.0"),sQuery(id+"F4.wireOp",EDGE,"E14.1")])]})]}),"instanceName":"1"});
            var Q2;
            Q2=makeQuery(id+"F16.opPattern","COPY",EDGE,{"derivedFrom":makeQuery(id+"F5.boolean.opBoolean","MERGE",EDGE,{"derivedFrom":[makeQuery(id+"F1.opExtrude","SWEPT_EDGE",EDGE,{"disambiguationData":[OSD([sQuery(id+"F0.wireOp",EDGE,"E1"),sQuery(id+"F0.wireOp",EDGE,"E2")])]}),makeQuery(id+"F5.opExtrude","SWEPT_EDGE",EDGE,{"disambiguationData":[OSD([sQuery(id+"F4.wireOp",EDGE,"E14.1"),sQuery(id+"F4.wireOp",EDGE,"E14.2")])]})]}),"instanceName":"1"});
            var Q3;
            Q3=makeQuery(id+"F5.boolean.opBoolean","MERGE",EDGE,{"derivedFrom":[makeQuery(id+"F1.opExtrude","SWEPT_EDGE",EDGE,{"disambiguationData":[OSD([sQuery(id+"F0.wireOp",EDGE,"E1"),sQuery(id+"F0.wireOp",EDGE,"E6.0.MirrorCS")])]}),makeQuery(id+"F5.opExtrude","SWEPT_EDGE",EDGE,{"disambiguationData":[OSD([sQuery(id+"F4.wireOp",EDGE,"E14.0"),sQuery(id+"F4.wireOp",EDGE,"E14.1")])]})]});
            var Q4;
            Q4=makeQuery(id+"F16.opPattern","COPY",EDGE,{"derivedFrom":makeQuery(id+"F5.boolean.opBoolean","MERGE",EDGE,{"derivedFrom":[makeQuery(id+"F1.opExtrude","SWEPT_EDGE",EDGE,{"disambiguationData":[OSD([sQuery(id+"F0.wireOp",EDGE,"E1"),sQuery(id+"F0.wireOp",EDGE,"E6.0.MirrorCS")])]}),makeQuery(id+"F5.opExtrude","SWEPT_EDGE",EDGE,{"disambiguationData":[OSD([sQuery(id+"F4.wireOp",EDGE,"E14.0"),sQuery(id+"F4.wireOp",EDGE,"E14.1")])]})]}),"instanceName":"2"});
            var Q5;
            Q5=makeQuery(id+"F16.opPattern","COPY",EDGE,{"derivedFrom":makeQuery(id+"F5.boolean.opBoolean","MERGE",EDGE,{"derivedFrom":[makeQuery(id+"F1.opExtrude","SWEPT_EDGE",EDGE,{"disambiguationData":[OSD([sQuery(id+"F0.wireOp",EDGE,"E1"),sQuery(id+"F0.wireOp",EDGE,"E2")])]}),makeQuery(id+"F5.opExtrude","SWEPT_EDGE",EDGE,{"disambiguationData":[OSD([sQuery(id+"F4.wireOp",EDGE,"E14.1"),sQuery(id+"F4.wireOp",EDGE,"E14.2")])]})]}),"instanceName":"2"});
            fillet(context, id + "F23", {"entities" : qUnion([Q0, Q1, Q2, Q3, Q4, Q5]), "radius" : 5 * mm, "tangentPropagation" : true, "allowEdgeOverflow" : false});
        }
        {
            var Q0;
            Q0=makeQuery(id+"F21.boolean.opBoolean","COPY",FACE,{"derivedFrom":makeQuery(id+"F21.opExtrude","CAP_FACE",FACE,{"disambiguationData":[OSD([sQuery(id+"F20.wireOp",EDGE,"E48.1.0")])],"isStart":false})});
            var sketch = newSketch(context, id + "F24", { "sketchPlane" : qUnion([Q0])});
            skCircle(sketch, "E49", {"center": v(0, 33.75) * mm, "radius": 2.45 * mm});
            skCircle(sketch, "E50.1.0", {"center": v(-29.23, -16.88) * mm, "radius": 2.45 * mm});
            skCircle(sketch, "E50.2.0", {"center": v(29.23, -16.87) * mm, "radius": 2.45 * mm});
            skPoint(sketch, "E50.center", {"position": v(0, 0) * mm});
            skSolve(sketch);
        }
        {
            var Q0;
            Q0 = qSketchRegion(id + "F24", true);
            extrude(context, id + "F25", {"entities" : qUnion([Q0]), "operationType" : NewBodyOperationType.REMOVE, "endBound" : BoundingType.THROUGH_ALL, "oppositeDirection" : true, "depth" : 25 * mm});
        }
    });
